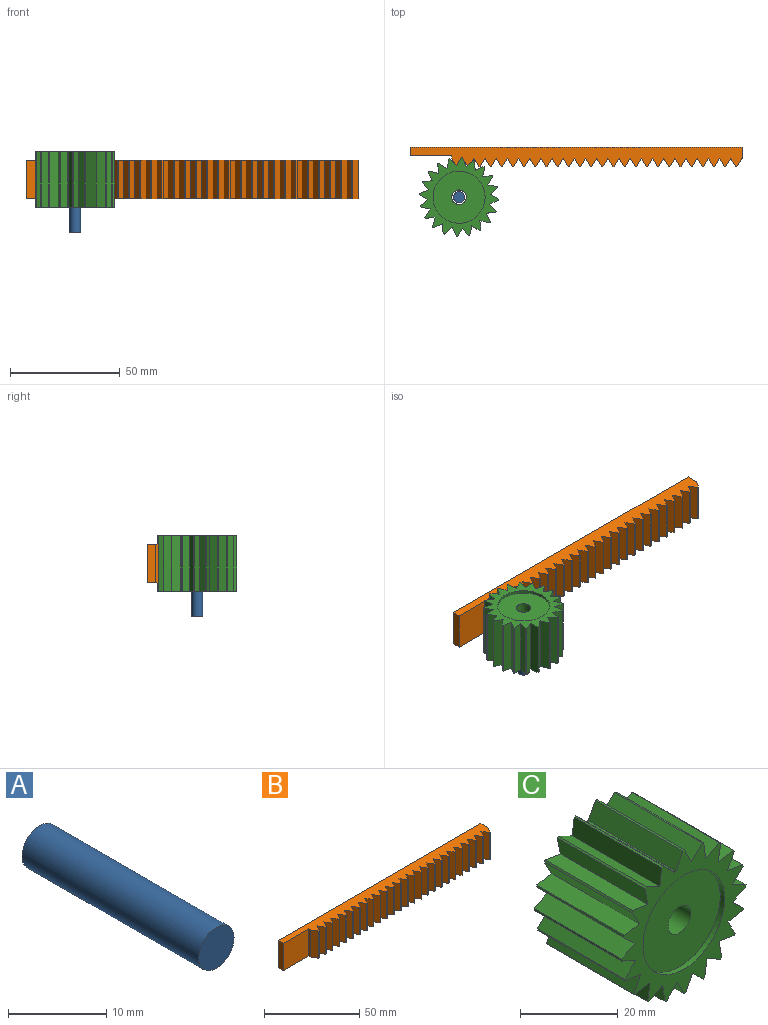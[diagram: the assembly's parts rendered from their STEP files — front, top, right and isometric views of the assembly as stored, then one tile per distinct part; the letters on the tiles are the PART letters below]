
ASSEMBLY  parts=3 mates=2
PART A: 3 faces, bbox 5.1x25.4x5.1 mm
  f0: cylinder r=2.54mm len=25.4mm, axis (0,1,0), area 405.4mm2, adj f1,f2
  f1: plane 5.08x5.08mm, normal (0,-1,0), area 20.3mm2, adj f0
  f2: plane 5.08x5.08mm, normal (0,1,0), area 20.3mm2, adj f0
PART B: 86 faces, bbox 151x9x17.5 mm
  f0: plane 17.45x0.04mm, normal (0,-1,0), area 0.8mm2, adj f1,f2,f7,f59
  f1: plane 151.03x9.04mm, normal (0,0,-1), area 1030.8mm2, adj f0,f3,f4,f5,f6,f7,f8,f9
  f2: plane 151.03x9.04mm, normal (0,0,1), area 1030.8mm2, adj f0,f3,f4,f5,f6,f7,f8,f9
  f3: plane 17.45x3.81mm, normal (-1,0,0), area 66.5mm2, adj f1,f2,f4,f5
  f4: plane 18.9x17.45mm, normal (0,-1,0), area 329.9mm2, adj f1,f2,f3,f6
  f5: plane 151.03x17.45mm, normal (0,1,0), area 2635.5mm2, adj f1,f2,f3,f7
  f6: plane 17.45x1.27mm, normal (-1,0,0), area 22.2mm2, adj f1,f2,f4,f13
  f7: plane 17.45x5.08mm, normal (1,0,0), area 88.6mm2, adj f0,f1,f2,f5
  f8: plane 17.45x3.96mm, normal (-0.87,-0.5,0), area 79.8mm2, adj f1,f2,f12,f84
  f9: plane 17.45x3.96mm, normal (0.87,-0.5,0), area 79.8mm2, adj f1,f2,f11,f84
  f10: plane 17.45x3.96mm, normal (0.87,-0.5,0), area 79.8mm2, adj f1,f2,f14,f83
  f11: plane 17.45x3.96mm, normal (-0.87,-0.5,0), area 79.8mm2, adj f1,f2,f9,f83
  f12: plane 17.45x3.96mm, normal (0.87,-0.5,0), area 79.8mm2, adj f1,f2,f8,f85
  f13: plane 17.45x3.96mm, normal (-0.87,-0.5,0), area 79.8mm2, adj f1,f2,f6,f85
  f14: plane 17.45x3.96mm, normal (-0.87,-0.5,0), area 79.8mm2, adj f1,f2,f10,f82
  f15: plane 17.45x3.96mm, normal (0.87,-0.5,0), area 79.8mm2, adj f1,f2,f17,f82
  f16: plane 17.45x3.96mm, normal (0.87,-0.5,0), area 79.8mm2, adj f1,f2,f18,f81
  f17: plane 17.45x3.96mm, normal (-0.87,-0.5,0), area 79.8mm2, adj f1,f2,f15,f81
  f18: plane 17.45x3.96mm, normal (-0.87,-0.5,0), area 79.8mm2, adj f1,f2,f16,f80
  f19: plane 17.45x3.96mm, normal (0.87,-0.5,0), area 79.8mm2, adj f1,f2,f21,f80
  f20: plane 17.45x3.96mm, normal (0.87,-0.5,0), area 79.8mm2, adj f1,f2,f22,f79
  f21: plane 17.45x3.96mm, normal (-0.87,-0.5,0), area 79.8mm2, adj f1,f2,f19,f79
  f22: plane 17.45x3.96mm, normal (-0.87,-0.5,0), area 79.8mm2, adj f1,f2,f20,f78
  f23: plane 17.45x3.96mm, normal (0.87,-0.5,0), area 79.8mm2, adj f1,f2,f25,f78
  f24: plane 17.45x3.96mm, normal (0.87,-0.5,0), area 79.8mm2, adj f1,f2,f26,f77
  f25: plane 17.45x3.96mm, normal (-0.87,-0.5,0), area 79.8mm2, adj f1,f2,f23,f77
  f26: plane 17.45x3.96mm, normal (-0.87,-0.5,0), area 79.8mm2, adj f1,f2,f24,f76
  f27: plane 17.45x3.96mm, normal (0.87,-0.5,0), area 79.8mm2, adj f1,f2,f29,f76
  f28: plane 17.45x3.96mm, normal (0.87,-0.5,0), area 79.8mm2, adj f1,f2,f30,f75
  f29: plane 17.45x3.96mm, normal (-0.87,-0.5,0), area 79.8mm2, adj f1,f2,f27,f75
  f30: plane 17.45x3.96mm, normal (-0.87,-0.5,0), area 79.8mm2, adj f1,f2,f28,f74
  f31: plane 17.45x3.96mm, normal (0.87,-0.5,0), area 79.8mm2, adj f1,f2,f33,f74
  f32: plane 17.45x3.96mm, normal (0.87,-0.5,0), area 79.8mm2, adj f1,f2,f34,f73
  f33: plane 17.45x3.96mm, normal (-0.87,-0.5,0), area 79.8mm2, adj f1,f2,f31,f73
  f34: plane 17.45x3.96mm, normal (-0.87,-0.5,0), area 79.8mm2, adj f1,f2,f32,f72
  f35: plane 17.45x3.96mm, normal (0.87,-0.5,0), area 79.8mm2, adj f1,f2,f37,f72
  f36: plane 17.45x3.96mm, normal (0.87,-0.5,0), area 79.8mm2, adj f1,f2,f38,f71
  f37: plane 17.45x3.96mm, normal (-0.87,-0.5,0), area 79.8mm2, adj f1,f2,f35,f71
  f38: plane 17.45x3.96mm, normal (-0.87,-0.5,0), area 79.8mm2, adj f1,f2,f36,f70
  f39: plane 17.45x3.96mm, normal (0.87,-0.5,0), area 79.8mm2, adj f1,f2,f41,f70
  f40: plane 17.45x3.96mm, normal (0.87,-0.5,0), area 79.8mm2, adj f1,f2,f42,f69
  f41: plane 17.45x3.96mm, normal (-0.87,-0.5,0), area 79.8mm2, adj f1,f2,f39,f69
  f42: plane 17.45x3.96mm, normal (-0.87,-0.5,0), area 79.8mm2, adj f1,f2,f40,f68
  f43: plane 17.45x3.96mm, normal (0.87,-0.5,0), area 79.8mm2, adj f1,f2,f45,f68
  f44: plane 17.45x3.96mm, normal (0.87,-0.5,0), area 79.8mm2, adj f1,f2,f46,f67
  f45: plane 17.45x3.96mm, normal (-0.87,-0.5,0), area 79.8mm2, adj f1,f2,f43,f67
  f46: plane 17.45x3.96mm, normal (-0.87,-0.5,0), area 79.8mm2, adj f1,f2,f44,f66
  f47: plane 17.45x3.96mm, normal (0.87,-0.5,0), area 79.8mm2, adj f1,f2,f49,f66
  f48: plane 17.45x3.96mm, normal (0.87,-0.5,0), area 79.8mm2, adj f1,f2,f50,f65
  f49: plane 17.45x3.96mm, normal (-0.87,-0.5,0), area 79.8mm2, adj f1,f2,f47,f65
  f50: plane 17.45x3.96mm, normal (-0.87,-0.5,0), area 79.8mm2, adj f1,f2,f48,f64
  f51: plane 17.45x3.96mm, normal (0.87,-0.5,0), area 79.8mm2, adj f1,f2,f53,f64
  f52: plane 17.45x3.96mm, normal (0.87,-0.5,0), area 79.8mm2, adj f1,f2,f54,f63
  f53: plane 17.45x3.96mm, normal (-0.87,-0.5,0), area 79.8mm2, adj f1,f2,f51,f63
  f54: plane 17.45x3.96mm, normal (-0.87,-0.5,0), area 79.8mm2, adj f1,f2,f52,f62
  f55: plane 17.45x3.96mm, normal (0.87,-0.5,0), area 79.8mm2, adj f1,f2,f57,f62
  f56: plane 17.45x3.96mm, normal (0.87,-0.5,0), area 79.8mm2, adj f1,f2,f58,f61
  f57: plane 17.45x3.96mm, normal (-0.87,-0.5,0), area 79.8mm2, adj f1,f2,f55,f61
  f58: plane 17.45x3.96mm, normal (-0.87,-0.5,0), area 79.8mm2, adj f1,f2,f56,f60
  f59: plane 17.45x3.96mm, normal (0.87,-0.5,0), area 79.8mm2, adj f0,f1,f2,f60
  f60: plane 17.45x0.51mm, normal (0,-1,0), area 8.9mm2, adj f1,f2,f58,f59
  f61: plane 17.45x0.51mm, normal (0,-1,0), area 8.9mm2, adj f1,f2,f56,f57
  f62: plane 17.45x0.51mm, normal (0,-1,0), area 8.9mm2, adj f1,f2,f54,f55
  f63: plane 17.45x0.51mm, normal (0,-1,0), area 8.9mm2, adj f1,f2,f52,f53
  f64: plane 17.45x0.51mm, normal (0,-1,0), area 8.9mm2, adj f1,f2,f50,f51
  f65: plane 17.45x0.51mm, normal (0,-1,0), area 8.9mm2, adj f1,f2,f48,f49
  f66: plane 17.45x0.51mm, normal (0,-1,0), area 8.9mm2, adj f1,f2,f46,f47
  f67: plane 17.45x0.51mm, normal (0,-1,0), area 8.9mm2, adj f1,f2,f44,f45
  f68: plane 17.45x0.51mm, normal (0,-1,0), area 8.9mm2, adj f1,f2,f42,f43
  f69: plane 17.45x0.51mm, normal (0,-1,0), area 8.9mm2, adj f1,f2,f40,f41
  f70: plane 17.45x0.51mm, normal (0,-1,0), area 8.9mm2, adj f1,f2,f38,f39
  f71: plane 17.45x0.51mm, normal (0,-1,0), area 8.9mm2, adj f1,f2,f36,f37
  f72: plane 17.45x0.51mm, normal (0,-1,0), area 8.9mm2, adj f1,f2,f34,f35
  f73: plane 17.45x0.51mm, normal (0,-1,0), area 8.9mm2, adj f1,f2,f32,f33
  f74: plane 17.45x0.51mm, normal (0,-1,0), area 8.9mm2, adj f1,f2,f30,f31
  f75: plane 17.45x0.51mm, normal (0,-1,0), area 8.9mm2, adj f1,f2,f28,f29
  f76: plane 17.45x0.51mm, normal (0,-1,0), area 8.9mm2, adj f1,f2,f26,f27
  f77: plane 17.45x0.51mm, normal (0,-1,0), area 8.9mm2, adj f1,f2,f24,f25
  f78: plane 17.45x0.51mm, normal (0,-1,0), area 8.9mm2, adj f1,f2,f22,f23
  f79: plane 17.45x0.51mm, normal (0,-1,0), area 8.9mm2, adj f1,f2,f20,f21
  f80: plane 17.45x0.51mm, normal (0,-1,0), area 8.9mm2, adj f1,f2,f18,f19
  f81: plane 17.45x0.51mm, normal (0,-1,0), area 8.9mm2, adj f1,f2,f16,f17
  f82: plane 17.45x0.51mm, normal (0,-1,0), area 8.9mm2, adj f1,f2,f14,f15
  f83: plane 17.45x0.51mm, normal (0,-1,0), area 8.9mm2, adj f1,f2,f10,f11
  f84: plane 17.45x0.51mm, normal (0,-1,0), area 8.9mm2, adj f1,f2,f8,f9
  f85: plane 17.45x0.51mm, normal (0,-1,0), area 8.9mm2, adj f1,f2,f12,f13
PART C: 68 faces, bbox 36.1x25.4x36.1 mm
  f0: cylinder r=3.3mm len=22.86mm, axis (0,-1,0), area 474.3mm2, adj f64,f66
  f1: plane 25.4x4.06mm, normal (-0.89,0,0.46), area 116.1mm2, adj f2,f42,f43,f63
  f2: cylinder r=14.18mm len=25.4mm, axis (0,1,0), area 10.3mm2, adj f1,f3,f42,f43
  f3: plane 25.4x3.23mm, normal (0.69,0,0.72), area 114.1mm2, adj f2,f42,f43,f44
  f4: plane 25.4x4.44mm, normal (-0.99,0,0.13), area 113.6mm2, adj f5,f42,f43,f44
  f5: plane 25.4x3.95mm, normal (0.44,0,0.9), area 111.7mm2, adj f4,f42,f43,f45
  f6: plane 25.4x4.4mm, normal (-0.98,0,-0.18), area 113.6mm2, adj f7,f42,f43,f45
  f7: plane 25.4x4.35mm, normal (0.14,0,0.99), area 111.7mm2, adj f6,f42,f43,f46
  f8: plane 25.4x3.93mm, normal (-0.88,0,-0.48), area 113.6mm2, adj f9,f42,f43,f46
  f9: plane 25.4x4.33mm, normal (-0.17,0,0.99), area 111.7mm2, adj f8,f42,f43,f47
  f10: plane 25.4x3.24mm, normal (-0.69,0,-0.72), area 113.6mm2, adj f11,f42,f43,f47
  f11: plane 25.4x3.9mm, normal (-0.46,0,0.89), area 111.7mm2, adj f10,f42,f43,f48
  f12: plane 25.4x4.03mm, normal (-0.43,0,-0.9), area 113.6mm2, adj f13,f42,f43,f48
  f13: plane 25.4x3.14mm, normal (-0.71,0,0.7), area 111.7mm2, adj f12,f42,f43,f49
  f14: plane 25.4x4.43mm, normal (-0.14,0,-0.99), area 113.6mm2, adj f15,f42,f43,f49
  f15: plane 25.4x3.93mm, normal (-0.89,0,0.45), area 111.7mm2, adj f14,f42,f43,f50
  f16: plane 25.4x4.4mm, normal (0.18,0,-0.98), area 113.6mm2, adj f17,f42,f43,f50
  f17: plane 25.4x4.35mm, normal (-0.99,0,0.15), area 111.7mm2, adj f16,f42,f43,f51
  f18: plane 25.4x3.95mm, normal (0.47,0,-0.88), area 113.6mm2, adj f19,f42,f43,f51
  f19: plane 25.4x4.34mm, normal (-0.99,0,-0.16), area 111.7mm2, adj f18,f42,f43,f52
  f20: plane 25.4x3.21mm, normal (0.72,0,-0.7), area 113.6mm2, adj f21,f42,f43,f52
  f21: plane 25.4x3.91mm, normal (-0.89,0,-0.46), area 111.7mm2, adj f20,f42,f43,f53
  f22: plane 25.4x4.01mm, normal (0.9,0,-0.44), area 113.6mm2, adj f23,f42,f43,f53
  f23: plane 25.4x3.11mm, normal (-0.71,0,-0.71), area 111.7mm2, adj f22,f42,f43,f54
  f24: plane 25.4x4.43mm, normal (0.99,0,-0.14), area 113.6mm2, adj f25,f42,f43,f54
  f25: plane 25.4x3.91mm, normal (-0.46,0,-0.89), area 111.7mm2, adj f24,f42,f43,f55
  f26: plane 25.4x4.41mm, normal (0.99,0,0.17), area 113.6mm2, adj f27,f42,f43,f55
  f27: plane 25.4x4.34mm, normal (-0.16,0,-0.99), area 111.7mm2, adj f26,f42,f43,f56
  f28: plane 25.4x3.97mm, normal (0.89,0,0.46), area 113.6mm2, adj f29,f42,f43,f56
  f29: plane 25.4x4.35mm, normal (0.15,0,-0.99), area 111.7mm2, adj f28,f42,f43,f57
  f30: plane 25.4x3.18mm, normal (0.7,0,0.71), area 113.6mm2, adj f31,f42,f43,f57
  f31: plane 25.4x3.93mm, normal (0.45,0,-0.89), area 111.7mm2, adj f30,f42,f43,f58
  f32: plane 25.4x3.99mm, normal (0.45,0,0.89), area 113.6mm2, adj f33,f42,f43,f58
  f33: plane 25.4x3.14mm, normal (0.7,0,-0.71), area 111.7mm2, adj f32,f42,f43,f59
  f34: plane 25.4x4.42mm, normal (0.15,0,0.99), area 113.6mm2, adj f35,f42,f43,f59
  f35: plane 25.4x3.89mm, normal (0.89,0,-0.46), area 111.7mm2, adj f34,f42,f43,f60
  f36: plane 25.4x4.42mm, normal (-0.16,0,0.99), area 113.6mm2, adj f37,f42,f43,f60
  f37: plane 25.4x4.33mm, normal (0.99,0,-0.17), area 111.7mm2, adj f36,f42,f43,f61
  f38: plane 25.4x3.99mm, normal (-0.45,0,0.89), area 113.6mm2, adj f39,f42,f43,f61
  f39: plane 25.4x4.35mm, normal (0.99,0,0.14), area 111.7mm2, adj f38,f42,f43,f62
  f40: plane 25.4x3.17mm, normal (-0.71,0,0.71), area 113.6mm2, adj f41,f42,f43,f62
  f41: plane 25.4x3.95mm, normal (0.9,0,0.44), area 111.7mm2, adj f40,f42,f43,f63
  f42: plane 36.09x36.09mm, normal (0,-1,0), area 381.6mm2, adj f1,f2,f3,f4,f5,f6,f7,f8
  f43: plane 36.09x36.09mm, normal (0,1,0), area 381.6mm2, adj f1,f2,f3,f4,f5,f6,f7,f8
  f44: plane 25.4x0.43mm, normal (-0.33,0,0.94), area 11.6mm2, adj f3,f4,f42,f43
  f45: plane 25.4x0.36mm, normal (-0.61,0,0.8), area 11.6mm2, adj f5,f6,f42,f43
  f46: plane 25.4x0.37mm, normal (-0.82,0,0.57), area 11.6mm2, adj f7,f8,f42,f43
  f47: plane 25.4x0.44mm, normal (-0.96,0,0.29), area 11.6mm2, adj f9,f10,f42,f43
  f48: plane 25.4x0.46mm, normal (-1,0,-0.02), area 11.6mm2, adj f11,f12,f42,f43
  f49: plane 25.4x0.43mm, normal (-0.95,0,-0.32), area 11.6mm2, adj f13,f14,f42,f43
  f50: plane 25.4x0.37mm, normal (-0.8,0,-0.6), area 11.6mm2, adj f15,f16,f42,f43
  f51: plane 25.4x0.37mm, normal (-0.58,0,-0.82), area 11.6mm2, adj f17,f18,f42,f43
  f52: plane 25.4x0.43mm, normal (-0.3,0,-0.95), area 11.6mm2, adj f19,f20,f42,f43
  f53: plane 25.4x0.46mm, normal (0.01,0,-1), area 11.6mm2, adj f21,f22,f42,f43
  f54: plane 25.4x0.43mm, normal (0.31,0,-0.95), area 11.6mm2, adj f23,f24,f42,f43
  f55: plane 25.4x0.37mm, normal (0.59,0,-0.81), area 11.6mm2, adj f25,f26,f42,f43
  f56: plane 25.4x0.37mm, normal (0.81,0,-0.59), area 11.6mm2, adj f27,f28,f42,f43
  f57: plane 25.4x0.43mm, normal (0.95,0,-0.31), area 11.6mm2, adj f29,f30,f42,f43
  f58: plane 25.4x0.46mm, normal (1,0,0), area 11.6mm2, adj f31,f32,f42,f43
  f59: plane 25.4x0.43mm, normal (0.95,0,0.31), area 11.6mm2, adj f33,f34,f42,f43
  f60: plane 25.4x0.37mm, normal (0.81,0,0.58), area 11.6mm2, adj f35,f36,f42,f43
  f61: plane 25.4x0.37mm, normal (0.59,0,0.8), area 11.6mm2, adj f37,f38,f42,f43
  f62: plane 25.4x0.43mm, normal (0.32,0,0.95), area 11.6mm2, adj f39,f40,f42,f43
  f63: plane 25.4x0.46mm, normal (0.01,0,1), area 11.6mm2, adj f1,f41,f42,f43
  f64: plane 23.68x23.68mm, normal (0,-1,0), area 406.1mm2, adj f0,f65
  f65: cylinder r=11.84mm len=23.68mm, axis (0,-1,0), area 94.5mm2, adj f42,f64
  f66: plane 23.68x23.68mm, normal (0,1,0), area 406.1mm2, adj f0,f67
  f67: cylinder r=11.84mm len=23.68mm, axis (0,1,0), area 94.5mm2, adj f43,f66
PLACE A rot(axis=(-1,-0.06,0.06),90.2deg) t=(-6.74,-22.82,2.19)mm
PLACE B t=(46.46,0,26.32)mm fixed
PLACE C rot(axis=(1,-0.03,-0.03),90deg) t=(-6.74,-22.82,39.02)mm
MATE slider B.f12 <-> C.f21  axis (0.87,-0.5,0) through (-6.21,-7.06,26.32)mm
MATE revolute A.f0 <-> C.f0  axis (0,0,-1) through (-6.74,-22.82,14.89)mm
